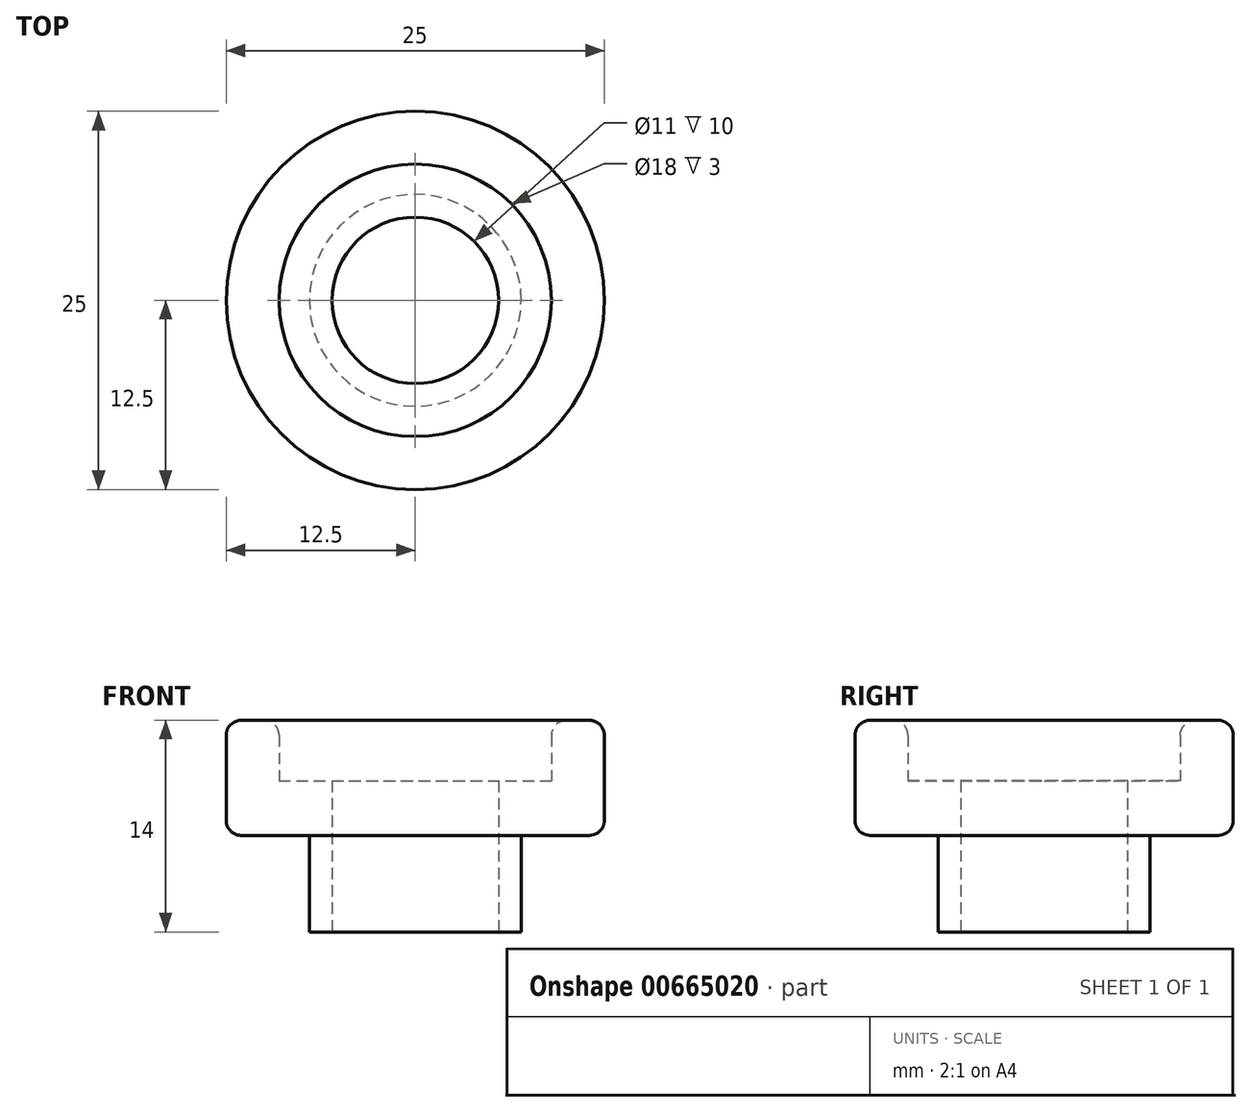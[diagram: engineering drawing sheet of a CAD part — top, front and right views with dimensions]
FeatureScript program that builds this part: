
annotation { "Feature Type Name" : "Feature", "Feature Type Description" : "" }
export const myFeature = defineFeature(function(context is Context, id is Id, definition is map)
    precondition{}
    {
        {
            var Q0;
            Q0=qCreatedBy(makeId("Front.planeOp"),FACE);
            var sketch = newSketch(context, id + "F0", { "sketchPlane" : qUnion([Q0])});
            skLineSegment(sketch, "E0", {"start": v(5.5, 0) * mm, "end": v(7, 0) * mm});
            skLineSegment(sketch, "E1", {"start": v(7, 0) * mm, "end": v(7, 6.39) * mm});
            skLineSegment(sketch, "E2", {"start": v(7, 6.39) * mm, "end": v(12.5, 6.39) * mm});
            skLineSegment(sketch, "E3", {"start": v(12.5, 6.39) * mm, "end": v(12.5, 14) * mm});
            skLineSegment(sketch, "E4", {"start": v(12.5, 14) * mm, "end": v(9, 14) * mm});
            skLineSegment(sketch, "E5", {"start": v(9, 14) * mm, "end": v(9, 10) * mm});
            skLineSegment(sketch, "E6", {"start": v(9, 10) * mm, "end": v(5.5, 10) * mm});
            skLineSegment(sketch, "E7", {"start": v(5.5, 10) * mm, "end": v(5.5, 0) * mm});
            skLineSegment(sketch, "E8", {"start": v(0, 0) * mm, "end": v(0, 19.45) * mm, "construction": true});
            skSolve(sketch);
        }
        {
            var Q0;
            Q0=makeQuery(id+"F0.imprint","IMPRINT",FACE,{"disambiguationData":[TD([[makeQuery(id+"F0.imprint","IMPRINT",EDGE,{"derivedFrom":sQuery(id+"F0.wireOp",EDGE,"E0")}),1.0]])]});
            var Q1;
            Q1=sQuery(id+"F0.wireOp",EDGE,"E8");
            revolve(context, id + "F1", {"surfaceOperationType" : NewSurfaceOperationType.NEW, "entities" : qUnion([Q0]), "axis" : qUnion([Q1]), "revolveType" : RevolveType.FULL});
        }
        {
            var Q0;
            Q0=makeQuery(id+"F1.opRevolve","SWEPT_EDGE",EDGE,{"disambiguationData":[OSD([sQuery(id+"F0.wireOp",EDGE,"E3"),sQuery(id+"F0.wireOp",EDGE,"E4")])]});
            var Q1;
            Q1=makeQuery(id+"F1.opRevolve","SWEPT_EDGE",EDGE,{"disambiguationData":[OSD([sQuery(id+"F0.wireOp",EDGE,"E4"),sQuery(id+"F0.wireOp",EDGE,"E5")])]});
            var Q2;
            Q2=makeQuery(id+"F1.opRevolve","SWEPT_EDGE",EDGE,{"disambiguationData":[OSD([sQuery(id+"F0.wireOp",EDGE,"E2"),sQuery(id+"F0.wireOp",EDGE,"E3")])]});
            fillet(context, id + "F2", {"entities" : qUnion([Q0, Q1, Q2]), "radius" : 1 * mm, "tangentPropagation" : true, "allowEdgeOverflow" : false});
        }
    });
